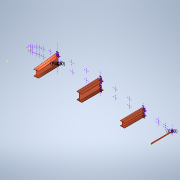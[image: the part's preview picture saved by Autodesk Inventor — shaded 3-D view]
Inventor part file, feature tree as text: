
AUTODESK INVENTOR PART (.ipt)
format: ipt  version: 2022 (Build 260153000, 153)  size: 399,360 bytes
history: native  units: mm
features: sketch x16, thicken_offset x12, loft x4, plane x1
ambient origin geometry x8: Origin, YZ Plane, XZ Plane, XY Plane, X Axis, Y Axis, Z Axis, Center Point
bodies: Body1 (feature_tree)
feature tree (33):
  sketch  "Sketch3"  dims[d29=150.0mm d35=2.0mm]
  sketch  "Sketch4"  dims[d36=90.0deg d37=2.0mm]
  sketch  "Sketch5"  dims[d38=90.0deg d43=2.0mm]
  sketch  "Sketch6"  dims[d44=2.0mm d51=2.0mm]
  plane  "Work Plane2"
  sketch  "Sketch9"  dims[d52=2.0mm]
  sketch  "Sketch10"  dims[d56=2.0mm]
  sketch  "Sketch14"  dims[d57=2.0mm]
  sketch  "Sketch15"  dims[d65=2.0mm]
  sketch  "Sketch16"  dims[d66=2.0mm]
  sketch  "Sketch17"  dims[d69=2.0mm]
  sketch  "Sketch18"  dims[d70=2.0mm]
  sketch  "Sketch19"  dims[d76=2.0mm]
  sketch  "Sketch20"  dims[d77=0.0mm]
  sketch  "Sketch21"  dims[d150=1.8mm]
  loft  "Loft2"
  loft  "Loft3"
  loft  "Loft4"
  thicken_offset  "Thicken2"
  thicken_offset  "Thicken3"
  thicken_offset  "Thicken4"
  thicken_offset  "Thicken5"
  thicken_offset  "Thicken6"
  thicken_offset  "Thicken7"
  thicken_offset  "Thicken8"
  thicken_offset  "Thicken9"
  thicken_offset  "Thicken10"
  thicken_offset  "Thicken12"
  thicken_offset  "Thicken13"
  thicken_offset  "Thicken14"
  loft  "Loft6"
  sketch  "Sketch22"  dims[d151=1.8mm]
  sketch  "Sketch23"  dims[d156=1.8mm d157=1.8mm d167=1.8mm d168=90.0deg d169=1.8mm d170=90.0deg d175=1.8mm d176=1.8mm d187=1.8mm d188=1.8mm d193=1.8mm d194=90.0deg d195=1.8mm d196=90.0deg d201=0.0mm d202=90.0deg d203=0.0mm d204=90.0deg d205=0.0mm d206=90.0deg d207=0.0mm d208=90.0deg d209=0.0mm d210=90.0deg d211=0.0mm d212=90.0deg d217=12.5mm d218=12.5mm d219=12.5mm d220=12.5mm d221=12.5mm d222=12.5mm d223=12.5mm d224=12.5mm d225=12.5mm d226=12.5mm d227=12.5mm d228=12.5mm d229=12.5mm d230=12.5mm d231=12.5mm d232=12.5mm d233=10.0mm d234=10.0mm d237=10.0mm d238=10.0mm d239=10.0mm d240=10.0mm d241=10.0mm d242=10.0mm d243=0.0mm d244=90.0deg d245=0.0mm d246=90.0deg d6=0.5mm d7=0.872665mm d8=0.5mm d9=0.872665mm]
